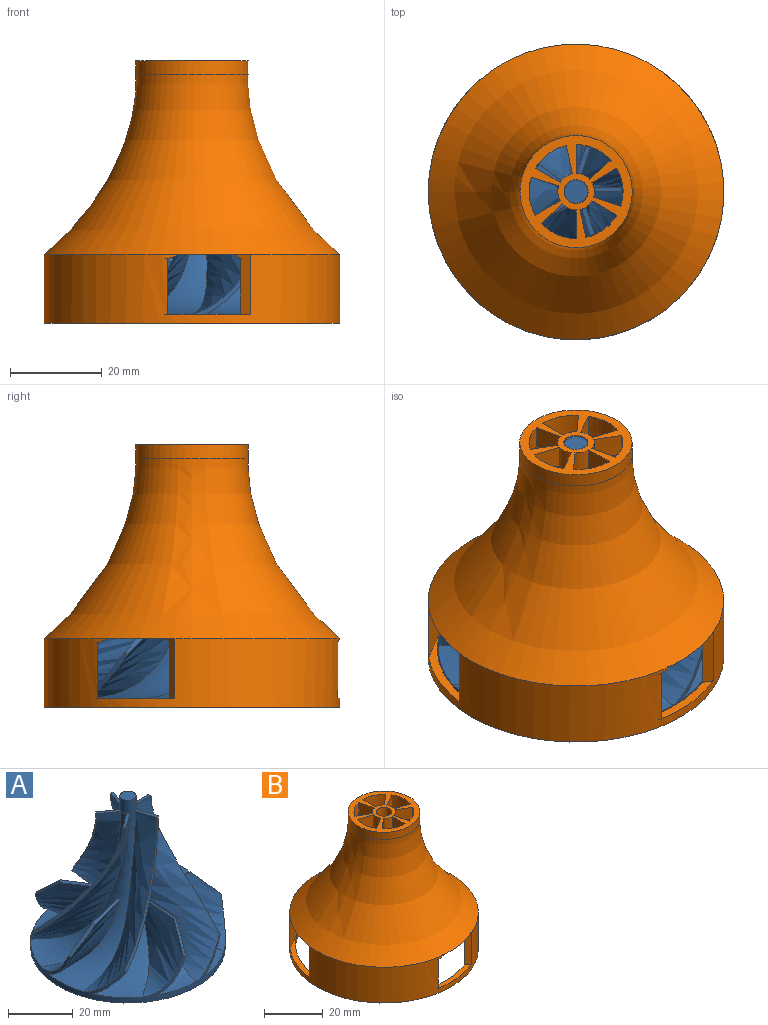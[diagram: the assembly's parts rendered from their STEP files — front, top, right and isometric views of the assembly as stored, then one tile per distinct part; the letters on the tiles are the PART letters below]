
ASSEMBLY  parts=2 mates=1
PART A: 54 faces, bbox 87.7x88.8x59 mm
  f0: revolved ~54.25x50mm, area 680.2mm2, adj f5,f17,f35,f44,f47,f48,f49
  f1: revolved ~58.39x50mm, area 680.2mm2, adj f5,f17,f27,f36,f39,f40,f41
  f2: revolved ~57.51x50mm, area 680.2mm2, adj f5,f14,f17,f28,f31,f32,f33
  f3: revolved ~52.46x50mm, area 680.2mm2, adj f5,f9,f13,f17,f19,f20,f21
  f4: revolved ~50x47.63mm, area 680.2mm2, adj f5,f10,f17,f23,f24,f25,f43
  f5: cylinder r=30mm len=60mm, axis (0,0,-1), area 529.9mm2, adj f0,f1,f2,f3,f4,f6,f7,f8
  f6: cylinder r=30mm len=8.38mm, axis (0,0,-1), area 7.6mm2, adj f5,f18,f20,f21
  f7: plane 60x60mm, normal (0,0,-1), area 2799.2mm2, adj f5,f50
  f8: bspline ~40.58x21.42mm, area 50.1mm2, adj f5,f9,f10,f11
  f9: offset ~52x42.99mm, area 667.3mm2, adj f3,f5,f8,f11
  f10: bspline ~50x40.99mm, area 693mm2, adj f4,f5,f8,f11
  f11: bspline ~8.68x6.69mm, area 7.6mm2, adj f8,f9,f10,f17
  f12: bspline ~40.58x26.19mm, area 50.1mm2, adj f5,f13,f14,f15
  f13: bspline ~50x41.13mm, area 693mm2, adj f3,f5,f12,f15
  f14: offset ~52x43.13mm, area 667.3mm2, adj f2,f5,f12,f15
  f15: bspline ~9.82x4.04mm, area 7.6mm2, adj f12,f13,f14,f17
  f16: plane 5x5mm, normal (0,0,1), area 19.6mm2, adj f17
  f17: cylinder r=2.5mm len=5mm, axis (0,0,-1), area 78.5mm2, adj f0,f1,f2,f3,f4,f11,f15,f16
  f18: bspline ~13.06x12.3mm, area 12.4mm2, adj f6,f19,f20,f21
  f19: bspline ~20.89x6.24mm, area 15.1mm2, adj f3,f18,f20,f21
  f20: bspline ~33.32x20mm, area 370.5mm2, adj f3,f5,f6,f18,f19
  f21: offset ~35.25x21.59mm, area 351.1mm2, adj f3,f5,f6,f18,f19
  f22: bspline ~13.49x12.3mm, area 12.4mm2, adj f5,f23,f24,f25
  f23: offset ~42x22mm, area 350.1mm2, adj f4,f5,f22,f25
  f24: bspline ~34.86x20mm, area 370.5mm2, adj f4,f5,f22,f25
  f25: bspline ~18.52x12.24mm, area 15.1mm2, adj f4,f22,f23,f24
  f26: bspline ~46.78x35.69mm, area 50.1mm2, adj f5,f27,f28,f29
  f27: offset ~52x42mm, area 667.3mm2, adj f1,f5,f26,f29
  f28: bspline ~50x40mm, area 693mm2, adj f2,f5,f26,f29
  f29: bspline ~10x1mm, area 7.6mm2, adj f17,f26,f27,f28
  f30: bspline ~12.3x11.55mm, area 12.4mm2, adj f5,f31,f32,f33
  f31: offset ~43.73x25.51mm, area 350.1mm2, adj f2,f5,f30,f33
  f32: bspline ~29.97x23.14mm, area 370.5mm2, adj f2,f5,f30,f33
  f33: bspline ~21.34x2.3mm, area 15.1mm2, adj f2,f30,f31,f32
  f34: bspline ~40.58x27.83mm, area 50.1mm2, adj f5,f35,f36,f37
  f35: offset ~52x46.72mm, area 667.3mm2, adj f0,f5,f34,f37
  f36: bspline ~50x44.72mm, area 693mm2, adj f1,f5,f34,f37
  f37: bspline ~7.64x3.33mm, area 7.6mm2, adj f17,f34,f35,f36
  f38: bspline ~12.3x10.48mm, area 12.4mm2, adj f5,f39,f40,f41
  f39: offset ~38.41x34.36mm, area 350.1mm2, adj f1,f5,f38,f41
  f40: bspline ~30.13x24.42mm, area 370.5mm2, adj f1,f5,f38,f41
  f41: bspline ~20.18x8.74mm, area 15.1mm2, adj f1,f38,f39,f40
  f42: bspline ~40.58x24.53mm, area 50.1mm2, adj f5,f43,f44,f45
  f43: offset ~52x47.06mm, area 667.3mm2, adj f4,f5,f42,f45
  f44: bspline ~50x45.06mm, area 693mm2, adj f0,f5,f42,f45
  f45: bspline ~8.68x6.69mm, area 7.6mm2, adj f17,f42,f43,f44
  f46: bspline ~8.91x8.67mm, area 12.4mm2, adj f5,f47,f48,f49
  f47: offset ~40.04x29.52mm, area 350.1mm2, adj f0,f5,f46,f49
  f48: bspline ~38.04x27.52mm, area 370.5mm2, adj f0,f5,f46,f49
  f49: bspline ~12.27x10.39mm, area 15.1mm2, adj f0,f46,f47,f48
  f50: cylinder r=3mm len=6mm, axis (0,0,-1), area 75.4mm2, adj f7,f51
  f51: plane 6x6mm, normal (0,0,-1), area 25.1mm2, adj f50,f52
  f52: cylinder r=1mm len=10mm, axis (0,0,-1), area 62.8mm2, adj f51,f53
  f53: plane 2x2mm, normal (0,0,-1), area 3.1mm2, adj f52
PART B: 51 faces, bbox 64.5x64.5x57.3 mm
  f0: cylinder r=30.25mm len=60.5mm, axis (0,0,-1), area 1706.4mm2, adj f1,f4,f33,f34,f37,f39,f40,f42
  f1: revolved ~60.5x60.5mm, area 4786.7mm2, adj f0,f2,f9,f13,f17,f21,f25,f29
  f2: plane 20.5x19.5mm, normal (0,0,-1), area 84.6mm2, adj f1,f3,f7,f8,f10,f11,f12,f14
  f3: cylinder r=2.62mm len=5.25mm, axis (0,0,1), area 82.5mm2, adj f2,f32
  f4: plane 64.5x64.5mm, normal (0,0,-1), area 392.7mm2, adj f0,f5
  f5: cylinder r=32.25mm len=64.5mm, axis (0,0,-1), area 2312.9mm2, adj f4,f6,f33,f34,f37,f39,f40,f42
  f6: revolved ~64.5x64.5mm, area 5516.4mm2, adj f5,f31,f34,f35,f40,f41,f45,f46
  f7: cylinder r=4mm len=5mm, axis (0,0,1), area 16.8mm2, adj f2,f8,f10,f32
  f8: plane 5x4.64mm, normal (-0.67,0.74,0), area 31.3mm2, adj f2,f7,f9,f32
  f9: cylinder r=10.25mm len=7.62mm, axis (0,0,1), area 42.9mm2, adj f1,f8,f10,f32
  f10: plane 6.25x5mm, normal (1,0,0), area 31.2mm2, adj f2,f7,f9,f32
  f11: cylinder r=4mm len=5mm, axis (0,0,1), area 16.8mm2, adj f2,f12,f14,f32
  f12: plane 6.11x5mm, normal (-0.98,-0.21,0), area 31.3mm2, adj f2,f11,f13,f32
  f13: cylinder r=10.25mm len=6.75mm, axis (0,0,1), area 42.9mm2, adj f1,f12,f14,f32
  f14: plane 5.41x5mm, normal (0.5,0.87,0), area 31.2mm2, adj f2,f11,f13,f32
  f15: cylinder r=4mm len=5mm, axis (0,0,1), area 16.8mm2, adj f2,f16,f18,f32
  f16: plane 5x4.64mm, normal (0.67,-0.74,0), area 31.3mm2, adj f2,f15,f17,f32
  f17: cylinder r=10.25mm len=7.62mm, axis (0,0,1), area 42.9mm2, adj f1,f16,f18,f32
  f18: plane 6.25x5mm, normal (-1,0,0), area 31.2mm2, adj f2,f15,f17,f32
  f19: cylinder r=4mm len=5mm, axis (0,0,1), area 16.8mm2, adj f2,f20,f22,f32
  f20: plane 5.94x5mm, normal (-0.31,-0.95,0), area 31.2mm2, adj f2,f19,f21,f32
  f21: cylinder r=10.25mm len=8.29mm, axis (0,0,1), area 42.9mm2, adj f1,f20,f22,f32
  f22: plane 5.41x5mm, normal (-0.5,0.87,0), area 31.2mm2, adj f2,f19,f21,f32
  f23: cylinder r=4mm len=5mm, axis (0,0,1), area 16.8mm2, adj f2,f24,f26,f32
  f24: plane 5.94x5mm, normal (0.31,0.95,0), area 31.2mm2, adj f2,f23,f25,f32
  f25: cylinder r=10.25mm len=8.29mm, axis (0,0,1), area 42.9mm2, adj f1,f24,f26,f32
  f26: plane 5.41x5mm, normal (0.5,-0.87,0), area 31.2mm2, adj f2,f23,f25,f32
  f27: cylinder r=4mm len=5mm, axis (0,0,1), area 16.8mm2, adj f2,f28,f30,f32
  f28: plane 6.11x5mm, normal (0.98,0.21,0), area 31.3mm2, adj f2,f27,f29,f32
  f29: cylinder r=10.25mm len=6.75mm, axis (0,0,1), area 42.9mm2, adj f1,f28,f30,f32
  f30: plane 5.41x5mm, normal (-0.5,-0.87,0), area 31.2mm2, adj f2,f27,f29,f32
  f31: cylinder r=12.24mm len=24.48mm, axis (0,0,-1), area 230.7mm2, adj f6,f32
  f32: plane 24.48x24.48mm, normal (0,0,1), area 225.2mm2, adj f3,f7,f8,f9,f10,f11,f12,f13
  f33: plane 25.87x11mm, normal (0,0,1), area 41.7mm2, adj f0,f5,f34,f37
  f34: plane 13.02x4mm, normal (1,0,0), area 33.7mm2, adj f0,f1,f5,f6,f33,f35
  f35: plane 25.51x9.9mm, normal (0,0,-1), area 55.5mm2, adj f1,f6,f34,f48
  f36: plane 1.04x0.9mm, normal (0,1,0), area 0mm2, adj f1,f37,f48
  f37: plane 12.05x11.18mm, normal (-1,0,0), area 134.7mm2, adj f0,f5,f33,f36,f48
  f38: plane 0.9x0.9mm, normal (-0.87,-0.5,0), area 0mm2, adj f1,f42,f49
  f39: plane 22.46x16.91mm, normal (0,0,1), area 41.7mm2, adj f0,f5,f40,f42
  f40: plane 13.02x3.47mm, normal (-0.5,0.87,0), area 33.7mm2, adj f0,f1,f5,f6,f39,f41
  f41: plane 21.33x17.14mm, normal (0,0,-1), area 55.5mm2, adj f1,f6,f40,f49
  f42: plane 12.05x9.68mm, normal (0.5,-0.87,0), area 134.7mm2, adj f0,f5,f38,f39,f49
  f43: plane 0.9x0.9mm, normal (0.87,-0.5,0), area 0mm2, adj f1,f47,f50
  f44: plane 27.91x6.05mm, normal (0,0,1), area 41.7mm2, adj f0,f5,f45,f47
  f45: plane 13.02x3.47mm, normal (-0.5,-0.87,0), area 33.7mm2, adj f0,f1,f5,f6,f44,f46
  f46: plane 27.04x6.81mm, normal (0,0,-1), area 55.5mm2, adj f1,f6,f45,f50
  f47: plane 12.05x9.68mm, normal (0.5,0.87,0), area 134.7mm2, adj f0,f5,f43,f44,f50
  f48: plane 13.72x1.1mm, normal (-0.65,0,-0.76), area 18.2mm2, adj f1,f5,f6,f35,f36,f37
  f49: plane 11.87x7.81mm, normal (0.33,-0.57,-0.76), area 18.2mm2, adj f1,f5,f6,f38,f41,f42
  f50: plane 12.42x6.84mm, normal (0.33,0.57,-0.76), area 18.2mm2, adj f1,f5,f6,f43,f46,f47
PLACE A t=(179.26,7.71,2.41)mm
PLACE B t=(79.26,7.71,2.41)mm fixed
MATE revolute A.f5 <-> B.f0  axis (0,0,-1) through (79.26,7.71,52.41)mm
